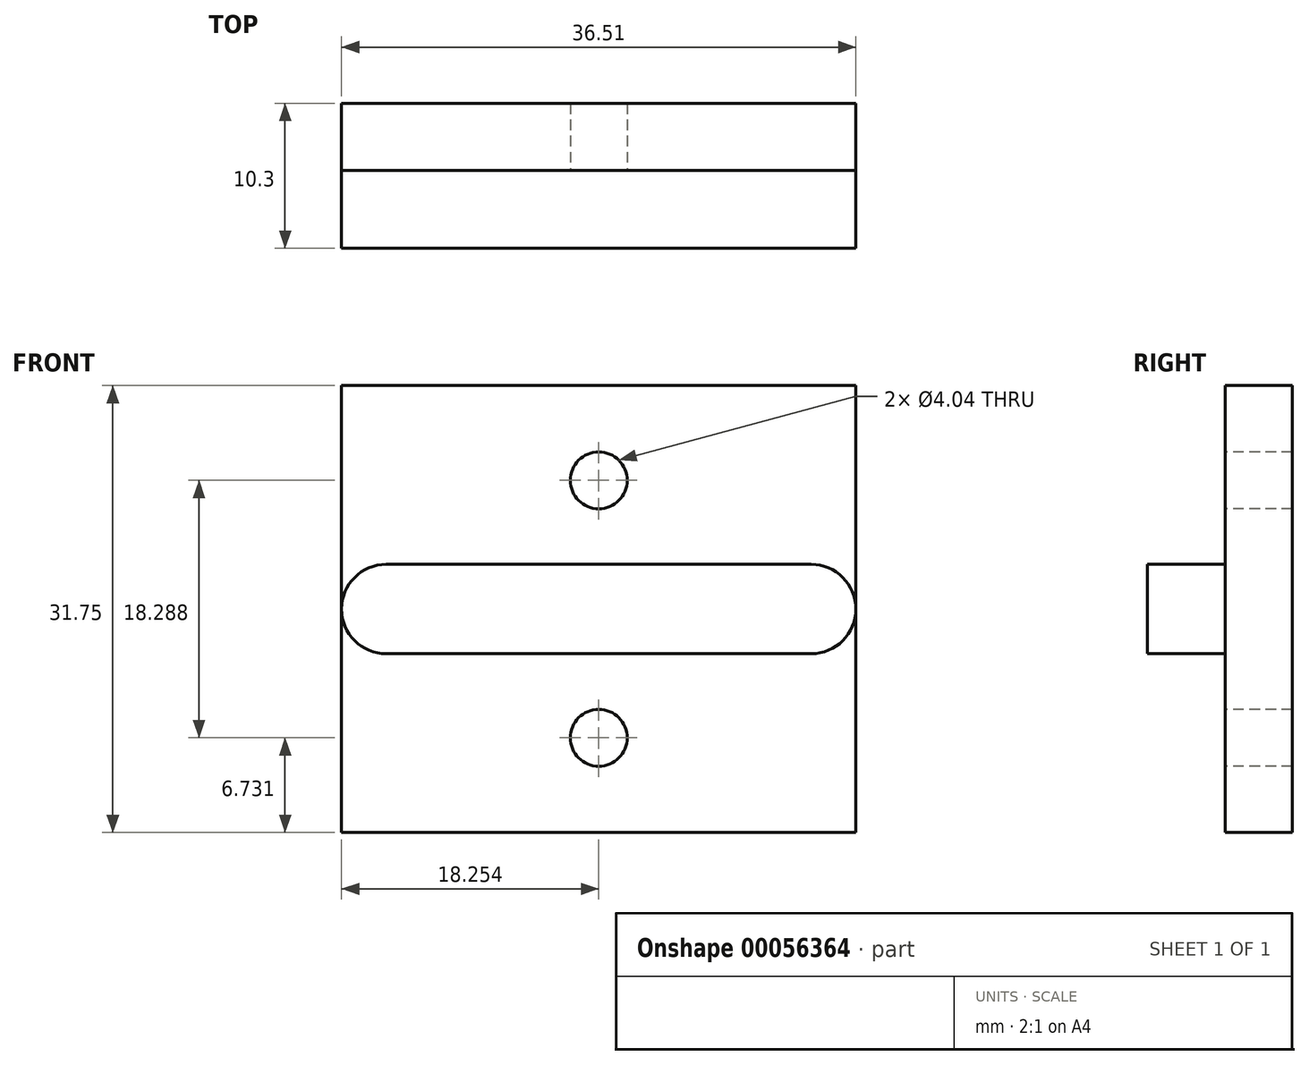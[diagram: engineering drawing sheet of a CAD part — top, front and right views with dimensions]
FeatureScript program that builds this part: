
annotation { "Feature Type Name" : "Feature", "Feature Type Description" : "" }
export const myFeature = defineFeature(function(context is Context, id is Id, definition is map)
    precondition{}
    {
        {
            var Q0;
            Q0=qCreatedBy(makeId("Right.planeOp"),FACE);
            var sketch = newSketch(context, id + "F0", { "sketchPlane" : qUnion([Q0])});
            skLineSegment(sketch, "E0", {"start": v(0, 0) * mm, "end": v(0, 31.75) * mm});
            skLineSegment(sketch, "E1", {"start": v(0, 31.75) * mm, "end": v(-4.76, 31.75) * mm});
            skLineSegment(sketch, "E2", {"start": v(-4.76, 31.75) * mm, "end": v(-4.76, 19.05) * mm});
            skLineSegment(sketch, "E3", {"start": v(-4.76, 19.05) * mm, "end": v(-10.3, 19.05) * mm});
            skLineSegment(sketch, "E4", {"start": v(-10.3, 19.05) * mm, "end": v(-10.3, 12.7) * mm});
            skLineSegment(sketch, "E5", {"start": v(-10.3, 12.7) * mm, "end": v(-4.76, 12.7) * mm});
            skLineSegment(sketch, "E6", {"start": v(-4.76, 12.7) * mm, "end": v(-4.76, 0) * mm});
            skLineSegment(sketch, "E7", {"start": v(-4.76, 0) * mm, "end": v(0, 0) * mm});
            skSolve(sketch);
        }
        {
            var Q0;
            Q0 = qSketchRegion(id + "F0", true);
            extrude(context, id + "F1", {"entities" : qUnion([Q0]), "oppositeDirection" : true, "depth" : 36.5 * mm});
        }
        {
            var Q0;
            Q0=makeQuery(id+"F1.opExtrude","SWEPT_FACE",FACE,{"disambiguationData":[OSD([sQuery(id+"F0.wireOp",EDGE,"E2")])]});
            var sketch = newSketch(context, id + "F2", { "sketchPlane" : qUnion([Q0])});
            skCircle(sketch, "E8", {"center": v(-18.26, 25.02) * mm, "radius": 2.02 * mm});
            skPoint(sketch, "E8.centerSnap0", {"position": v(-18.26, 31.75) * mm});
            skCircle(sketch, "E9", {"center": v(-18.26, 6.73) * mm, "radius": 2.02 * mm});
            skPoint(sketch, "E9.centerSnap0", {"position": v(-18.26, 19.05) * mm});
            skSolve(sketch);
        }
        {
            var Q0;
            Q0 = qSketchRegion(id + "F2", true);
            extrude(context, id + "F3", {"entities" : qUnion([Q0]), "operationType" : NewBodyOperationType.REMOVE, "endBound" : BoundingType.UP_TO_NEXT, "oppositeDirection" : true, "depth" : 25.4 * mm});
        }
        {
            var Q0;
            Q0=makeQuery(id+"F1.opExtrude","CAP_EDGE",EDGE,{"disambiguationData":[OSD([sQuery(id+"F0.wireOp",EDGE,"E3")])],"isStart":true});
            var Q1;
            Q1=makeQuery(id+"F1.opExtrude","CAP_EDGE",EDGE,{"disambiguationData":[OSD([sQuery(id+"F0.wireOp",EDGE,"E5")])],"isStart":true});
            var Q2;
            Q2=makeQuery(id+"F1.opExtrude","CAP_EDGE",EDGE,{"disambiguationData":[OSD([sQuery(id+"F0.wireOp",EDGE,"E5")])],"isStart":false});
            var Q3;
            Q3=makeQuery(id+"F1.opExtrude","CAP_EDGE",EDGE,{"disambiguationData":[OSD([sQuery(id+"F0.wireOp",EDGE,"E3")])],"isStart":false});
            fillet(context, id + "F4", {"entities" : qUnion([Q0, Q1, Q2, Q3]), "radius" : 3.17 * mm, "tangentPropagation" : true, "allowEdgeOverflow" : false});
        }
    });
